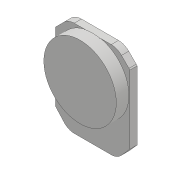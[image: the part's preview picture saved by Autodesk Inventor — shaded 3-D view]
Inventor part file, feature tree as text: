
AUTODESK INVENTOR PART (.ipt)
format: ipt  version: 2018 (Build 220112000, 112)  size: 113,152 bytes
history: native  units: mm
features: other x4, extrude x3, sketch x3, plane x1, reference x1
ambient origin geometry x8: Origin, YZ Plane, XZ Plane, XY Plane, X Axis, Y Axis, Z Axis, Center Point
bodies: Solid1 (feature_tree)
feature tree (12):
  extrude  "Extrusion1"  Depth=7.0mm TaperAngle=0.0deg
  extrude  "Extrusion2"  Depth=4.0mm TaperAngle=0.0deg
  sketch  "Sketch10"  dims[d44=10.0mm d45=0.0mm]
  plane  "Work Plane1"
  extrude  "Extrusion7"  [1 undecoded]
  sketch  "Sketch1"  dims[d0=40.0mm d1=7.0mm d2=0.0mm]
  sketch  "Sketch2"  dims[d3=80.4mm d4=4.0mm d5=0.0mm]
  reference  "Reference3"
  parser-record x1  (decoder bookkeeping rows leaked as tree rows — omitted from the tree; the rows remain in map.json)
  other  "servocheck.iam"
  other  "bottomarm:1"
  other  "arm1:1"
note: 1 required parameter value undecoded (feature->parameter linkage not recoverable at this tier; creation-order binding heuristic only, values carry confidence <= 0.55)
note: 1 file-system path scrubbed to <path> (originals preserved in map.json)
